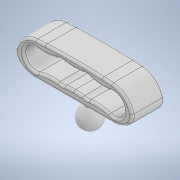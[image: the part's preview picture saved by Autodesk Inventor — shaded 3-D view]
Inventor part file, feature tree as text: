
AUTODESK INVENTOR PART (.ipt)
format: ipt  version: 2021 (Build 250183000, 183)  size: 410,112 bytes
history: native  units: in
note: dims shown in document units (in); Inventor stores cm internally (conversion verified against a paired STEP export)
features: fillet x7, sketch x2, revolve x1, extrude x1
ambient origin geometry x8: Origin, YZ Plane, XZ Plane, XY Plane, X Axis, Y Axis, Z Axis, Center Point
bodies: Solid1 (feature_tree)
feature tree (11):
  revolve  "Revolution1"  [1 undecoded]
  extrude  "Extrusion1"  Depth=1.1811in TaperAngle=0.0deg
  fillet  "Fillet2"  Radius=0.0206in
  fillet  "Fillet3"  Radius=0.7874in
  fillet  "Fillet4"  Radius=19.685in
  fillet  "Fillet5"  Radius=0.7874in
  fillet  "Fillet6"  Radius=0.3937in
  fillet  "Fillet7"  Radius=0.0787in
  fillet  "Fillet8"  Radius=0.0787in
  sketch  "Sketch1"  dims[d1=0.3937in d2=0.1476in]
  sketch  "Sketch2"  dims[d3=90.0deg d4=1.1811in d5=0.0in d10=0.0206in d12=0.7874in d13=19.685in d14=0.7874in d15=0.3937in d16=0.0787in d17=0.0787in d18=0.0787in]
note: 1 required parameter value undecoded (feature->parameter linkage not recoverable at this tier; creation-order binding heuristic only, values carry confidence <= 0.55)
